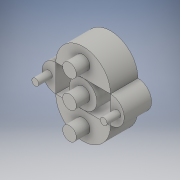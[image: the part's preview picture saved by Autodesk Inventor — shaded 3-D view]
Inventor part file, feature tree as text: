
AUTODESK INVENTOR PART (.ipt)
format: ipt  version: 2016 (Build 200138000, 138)  size: 155,136 bytes
history: native  units: in
note: dims shown in document units (in); Inventor stores cm internally (conversion verified against a paired STEP export)
features: extrude x4, sketch x4
ambient origin geometry x8: Origin, YZ Plane, XZ Plane, XY Plane, X Axis, Y Axis, Z Axis, Center Point
bodies: Solid1 (feature_tree)
feature tree (8):
  extrude  "Extrusion1"  Depth=1.0in
  extrude  "Extrusion2"  Depth=0.25in
  extrude  "Extrusion3"  Depth=0.25in
  extrude  "Extrusion4"  Depth=0.25in TaperAngle=0.0deg
  sketch  "Sketch1"  dims[d0=0.5in d1=1.0in]
  sketch  "Sketch2"  dims[d2=0.5in d3=0.0in d4=0.25in]
  sketch  "Sketch3"  dims[d5=0.25in d6=0.25in]
  sketch  "Sketch4"  dims[d7=0.25in d8=0.25in d9=0.0in d10=0.125in d11=0.125in d12=0.125in d13=0.125in d14=0.25in d15=0.0in d16=0.25in d17=0.25in d18=0.0in]
